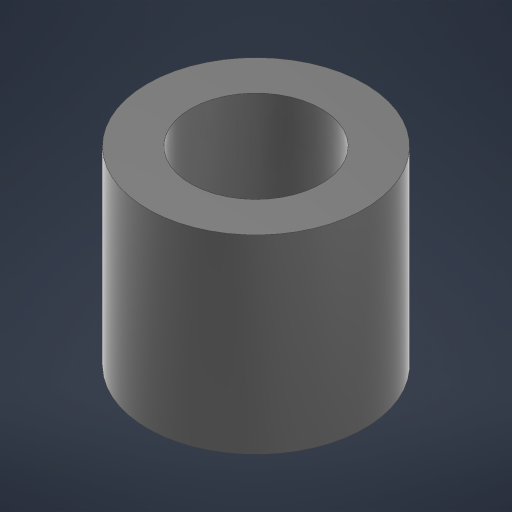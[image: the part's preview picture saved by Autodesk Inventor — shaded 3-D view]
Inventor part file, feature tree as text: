
AUTODESK INVENTOR PART (.ipt)
format: ipt  version: 2024.2 (Build 282272000, 272)  size: 171,520 bytes
history: native  units: mm
features: extrude x1, sketch x1, other x1
ambient origin geometry x8: Origin, YZ Plane, XZ Plane, XY Plane, X Axis, Y Axis, Z Axis, Center Point
bodies: Solid1 (feature_tree)
feature tree (3):
  extrude  "Extrusion1"  Depth=3.5mm
  sketch  "Sketch1"  dims[d0=2.4mm d1=4.0mm d2=3.5mm d3=0.0mm]
  other  "Finish1"
